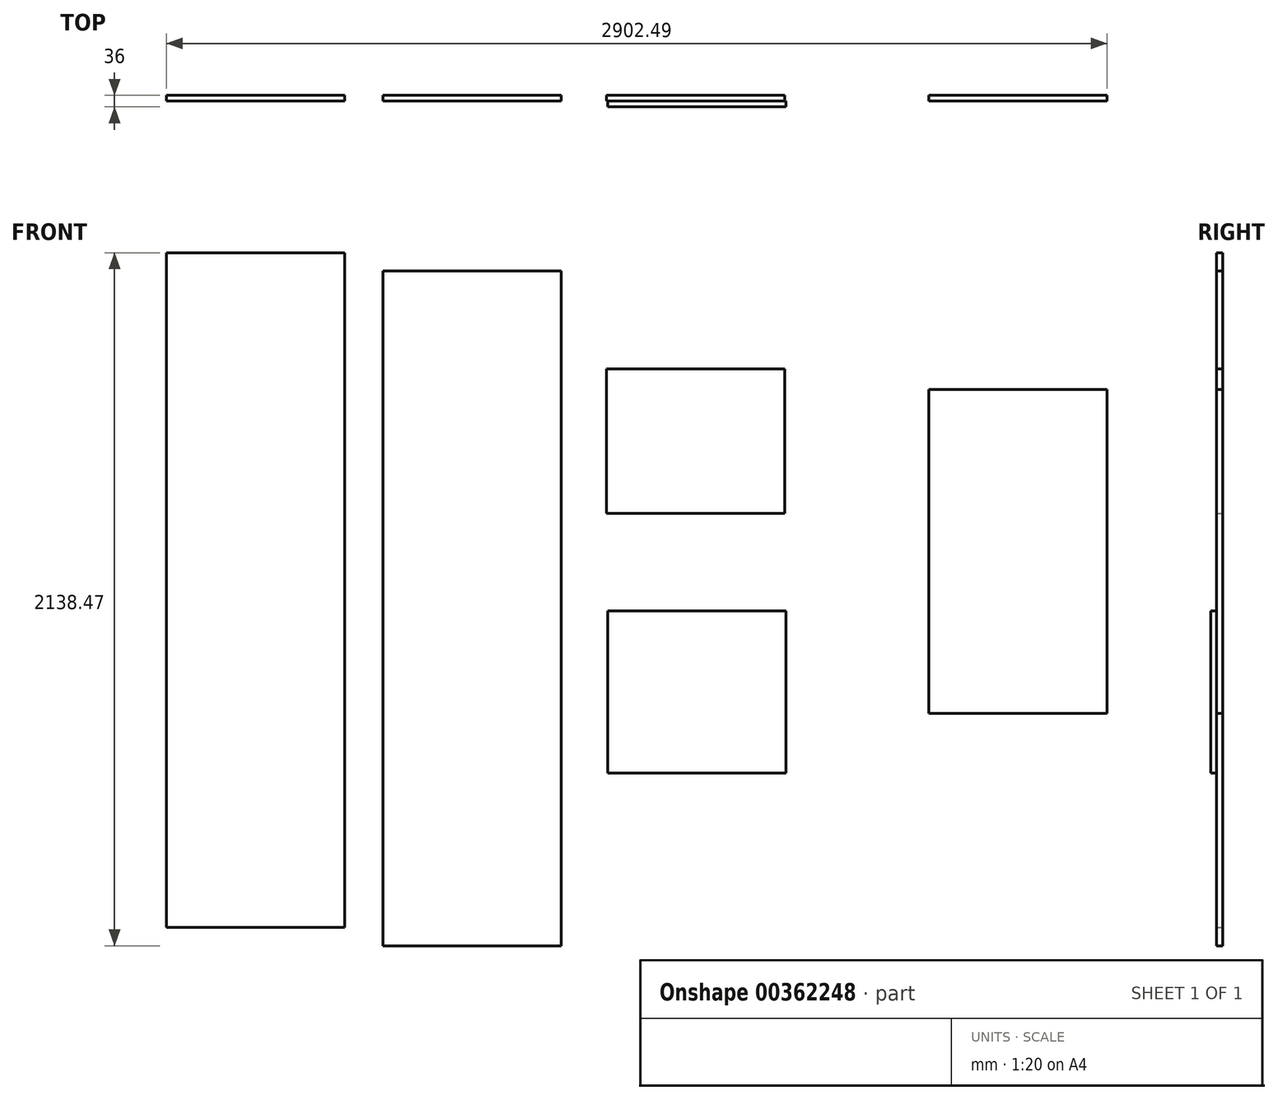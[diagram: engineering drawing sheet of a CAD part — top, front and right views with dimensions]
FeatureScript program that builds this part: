
annotation { "Feature Type Name" : "Feature", "Feature Type Description" : "" }
export const myFeature = defineFeature(function(context is Context, id is Id, definition is map)
    precondition{}
    {
        {
            var Q0;
            Q0=qCreatedBy(makeId("Front.planeOp"),FACE);
            var sketch = newSketch(context, id + "F0", { "sketchPlane" : qUnion([Q0])});
            skLineSegment(sketch, "E0.bottom", {"start": v(-306.68, 1108.55) * mm, "end": v(243.32, 1108.55) * mm});
            skLineSegment(sketch, "E0.top", {"start": v(-306.68, -973.45) * mm, "end": v(243.32, -973.45) * mm});
            skLineSegment(sketch, "E0.left", {"start": v(-306.68, 1108.55) * mm, "end": v(-306.68, -973.45) * mm});
            skLineSegment(sketch, "E0.right", {"start": v(243.32, 1108.55) * mm, "end": v(243.32, -973.45) * mm});
            skSolve(sketch);
        }
        {
            var Q0;
            Q0 = qSketchRegion(id + "F0", true);
            extrude(context, id + "F1", {"entities" : qUnion([Q0]), "depth" : 18 * mm});
        }
        {
            var Q0;
            Q0=qCreatedBy(makeId("Front.planeOp"),FACE);
            var sketch = newSketch(context, id + "F2", { "sketchPlane" : qUnion([Q0])});
            skLineSegment(sketch, "E1.bottom", {"start": v(-425.23, -916.98) * mm, "end": v(-975.23, -916.98) * mm});
            skLineSegment(sketch, "E1.top", {"start": v(-425.23, 1165.02) * mm, "end": v(-975.23, 1165.02) * mm});
            skLineSegment(sketch, "E1.left", {"start": v(-425.23, -916.98) * mm, "end": v(-425.23, 1165.02) * mm});
            skLineSegment(sketch, "E1.right", {"start": v(-975.23, -916.98) * mm, "end": v(-975.23, 1165.02) * mm});
            skSolve(sketch);
        }
        {
            var Q0;
            Q0 = qSketchRegion(id + "F2", true);
            extrude(context, id + "F3", {"entities" : qUnion([Q0]), "depth" : 18 * mm});
        }
        {
            var Q0;
            Q0=qCreatedBy(makeId("Front.planeOp"),FACE);
            var sketch = newSketch(context, id + "F4", { "sketchPlane" : qUnion([Q0])});
            skLineSegment(sketch, "E2.bottom", {"start": v(382.77, 807.08) * mm, "end": v(932.77, 807.08) * mm});
            skLineSegment(sketch, "E2.top", {"start": v(382.77, 361.08) * mm, "end": v(932.77, 361.08) * mm});
            skLineSegment(sketch, "E2.left", {"start": v(382.77, 807.08) * mm, "end": v(382.77, 361.08) * mm});
            skLineSegment(sketch, "E2.right", {"start": v(932.77, 807.08) * mm, "end": v(932.77, 361.08) * mm});
            skSolve(sketch);
        }
        {
            var Q0;
            Q0 = qSketchRegion(id + "F4", true);
            extrude(context, id + "F5", {"entities" : qUnion([Q0]), "depth" : 18 * mm});
        }
        {
            var Q0;
            Q0=makeQuery(id+"F5.opExtrude","CAP_FACE",FACE,{"disambiguationData":[OSD([sQuery(id+"F4.wireOp",EDGE,"E2.bottom"),sQuery(id+"F4.wireOp",EDGE,"E2.top"),sQuery(id+"F4.wireOp",EDGE,"E2.left"),sQuery(id+"F4.wireOp",EDGE,"E2.right")])],"isStart":false});
            var sketch = newSketch(context, id + "F6", { "sketchPlane" : qUnion([Q0])});
            skLineSegment(sketch, "E3.bottom", {"start": v(386.1, 59.27) * mm, "end": v(936.1, 59.27) * mm});
            skLineSegment(sketch, "E3.top", {"start": v(386.1, -440.73) * mm, "end": v(936.1, -440.73) * mm});
            skLineSegment(sketch, "E3.left", {"start": v(386.1, 59.27) * mm, "end": v(386.1, -440.73) * mm});
            skLineSegment(sketch, "E3.right", {"start": v(936.1, 59.27) * mm, "end": v(936.1, -440.73) * mm});
            skSolve(sketch);
        }
        {
            var Q0;
            Q0 = qSketchRegion(id + "F6", true);
            extrude(context, id + "F7", {"entities" : qUnion([Q0]), "depth" : 18 * mm});
        }
        {
            var Q0;
            Q0=qCreatedBy(makeId("Front.planeOp"),FACE);
            var sketch = newSketch(context, id + "F8", { "sketchPlane" : qUnion([Q0])});
            skLineSegment(sketch, "E4.bottom", {"start": v(1377.26, 743.25) * mm, "end": v(1927.26, 743.25) * mm});
            skLineSegment(sketch, "E4.top", {"start": v(1377.26, -256.75) * mm, "end": v(1927.26, -256.75) * mm});
            skLineSegment(sketch, "E4.left", {"start": v(1377.26, 743.25) * mm, "end": v(1377.26, -256.75) * mm});
            skLineSegment(sketch, "E4.right", {"start": v(1927.26, 743.25) * mm, "end": v(1927.26, -256.75) * mm});
            skSolve(sketch);
        }
        {
            var Q0;
            Q0 = qSketchRegion(id + "F8", true);
            extrude(context, id + "F9", {"entities" : qUnion([Q0]), "depth" : 18 * mm});
        }
    });
